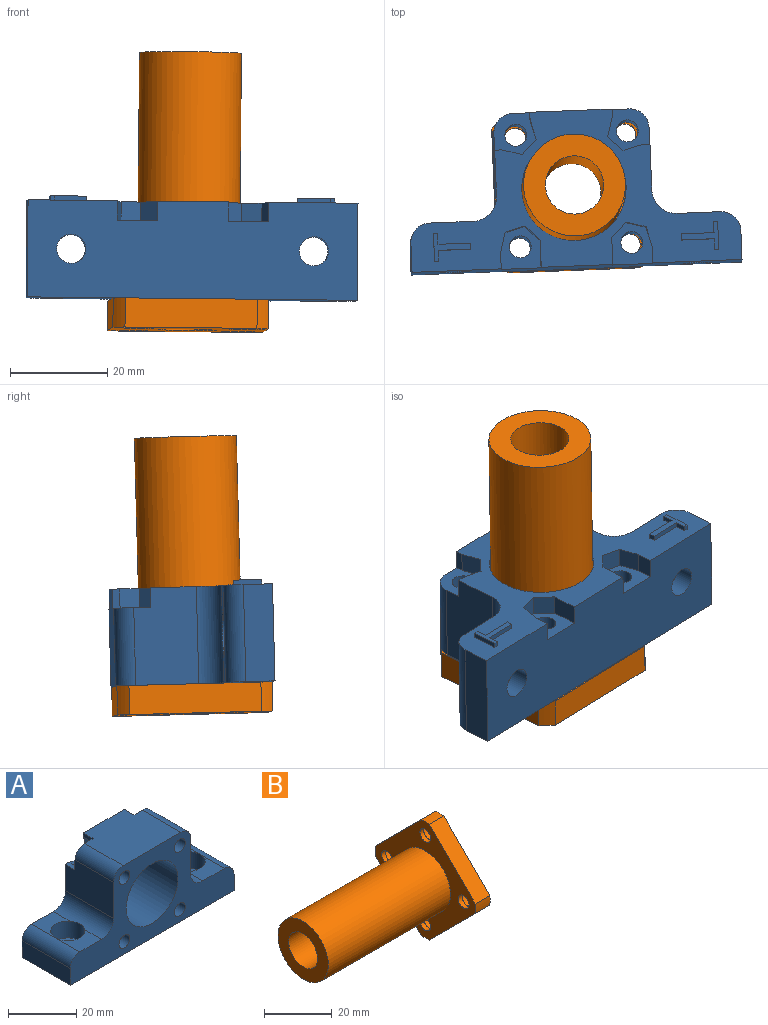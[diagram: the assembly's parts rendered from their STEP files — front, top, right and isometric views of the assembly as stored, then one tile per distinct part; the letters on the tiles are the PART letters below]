
ASSEMBLY  parts=2 mates=1
PART A: 70 faces, bbox 68x21x32 mm
  f0: cylinder r=4mm len=20mm, axis (0,-1,0), area 125.7mm2, adj f1,f2,f45,f51
  f1: plane 20x6mm, normal (1,0,0), area 120mm2, adj f0,f2,f37,f51
  f2: plane 68x32mm, normal (0,-1,0), area 954.3mm2, adj f0,f1,f3,f4,f5,f6,f7,f9
  f3: cylinder r=4mm len=20mm, axis (0,1,0), area 125.7mm2, adj f2,f4,f5,f14,f51
  f4: plane 10x9mm, normal (0,0,1), area 52.8mm2, adj f2,f3,f13,f41
  f5: plane 20x6mm, normal (-1,0,0), area 120mm2, adj f2,f3,f37,f51
  f6: cylinder r=4mm len=16mm, axis (0,1,0), area 100.5mm2, adj f2,f7,f8,f38
  f7: plane 24x20mm, normal (0,0,1), area 451.8mm2, adj f2,f6,f8,f9,f11,f29,f33,f51
  f8: plane 8.63x8.63mm, normal (0,1,0), area 42.7mm2, adj f6,f7,f32,f33,f34,f35,f36,f38
  f9: cylinder r=4mm len=16mm, axis (0,1,0), area 100.5mm2, adj f2,f7,f10,f11
  f10: plane 20x13mm, normal (-1,0,0), area 245.9mm2, adj f2,f9,f11,f13,f28,f51
  f11: plane 8.63x8.63mm, normal (0,1,0), area 42.7mm2, adj f7,f9,f10,f27,f28,f29,f30,f31
  f12: cylinder r=5mm len=20mm, axis (0,1,0), area 153mm2, adj f2,f38,f43,f45,f51
  f13: cylinder r=5mm len=20mm, axis (0,-1,0), area 154.1mm2, adj f2,f4,f10,f14,f41,f51
  f14: plane 10x9mm, normal (0,0,1), area 52.8mm2, adj f3,f13,f41,f51
  f15: plane 4.13x4mm, normal (0.26,0,-0.97), area 17.1mm2, adj f16,f19,f20,f51
  f16: plane 4x3.02mm, normal (-0.71,0,-0.71), area 17.1mm2, adj f15,f17,f20,f51
  f17: plane 5.61x4mm, normal (-1,0,0), area 22.4mm2, adj f16,f20,f37,f51
  f18: plane 4x3.39mm, normal (1,0,0), area 13.6mm2, adj f19,f20,f37,f51
  f19: plane 4.13x4mm, normal (0.97,0,-0.26), area 17.1mm2, adj f15,f18,f20,f51
  f20: plane 8.63x8.25mm, normal (0,1,0), area 44.9mm2, adj f15,f16,f17,f18,f19,f37,f46
  f21: plane 4.13x4mm, normal (-0.97,0,-0.26), area 17.1mm2, adj f22,f25,f26,f51
  f22: plane 4x3.39mm, normal (-1,0,0), area 13.6mm2, adj f21,f26,f37,f51
  f23: plane 5.61x4mm, normal (1,0,0), area 22.4mm2, adj f24,f26,f37,f51
  f24: plane 4x3.02mm, normal (0.71,0,-0.71), area 17.1mm2, adj f23,f25,f26,f51
  f25: plane 4.13x4mm, normal (-0.26,0,-0.97), area 17.1mm2, adj f21,f24,f26,f51
  f26: plane 8.63x8.25mm, normal (0,1,0), area 44.9mm2, adj f21,f22,f23,f24,f25,f37,f47
  f27: plane 4.13x4mm, normal (0.26,0,0.97), area 17.1mm2, adj f11,f28,f31,f51
  f28: plane 4x1.48mm, normal (0,0,1), area 5.9mm2, adj f10,f11,f27,f51
  f29: plane 4x1.48mm, normal (-1,0,0), area 5.9mm2, adj f7,f11,f30,f51
  f30: plane 4.13x4mm, normal (-0.97,0,-0.26), area 17.1mm2, adj f11,f29,f31,f51
  f31: plane 4x3.02mm, normal (-0.71,0,0.71), area 17.1mm2, adj f11,f27,f30,f51
  f32: plane 4.13x4mm, normal (0.97,0,-0.26), area 17.1mm2, adj f8,f33,f36,f51
  f33: plane 4x1.48mm, normal (1,0,0), area 5.9mm2, adj f7,f8,f32,f51
  f34: plane 4x1.48mm, normal (0,0,1), area 5.9mm2, adj f8,f35,f38,f51
  f35: plane 4.13x4mm, normal (-0.26,0,0.97), area 17.1mm2, adj f8,f34,f36,f51
  f36: plane 4x3.02mm, normal (0.71,0,0.71), area 17.1mm2, adj f8,f32,f35,f51
  f37: plane 68x20mm, normal (0,0,-1), area 1237.4mm2, adj f1,f2,f5,f17,f18,f20,f22,f23
  f38: plane 20x13mm, normal (1,0,0), area 245.9mm2, adj f2,f6,f8,f12,f34,f51
  f39: cylinder r=3mm len=6mm, axis (0,0,-1), area 75.4mm2, adj f37,f44
  f40: cylinder r=3mm len=6mm, axis (0,0,-1), area 75.4mm2, adj f37,f42
  f41: cylinder r=5mm len=10mm, axis (0,0,-1), area 188.8mm2, adj f4,f13,f14,f42
  f42: plane 10x10mm, normal (0,0,1), area 50.3mm2, adj f40,f41
  f43: cylinder r=5mm len=10mm, axis (0,0,-1), area 188.5mm2, adj f12,f44,f45
  f44: plane 10x10mm, normal (0,0,1), area 50.3mm2, adj f39,f43
  f45: plane 20x9mm, normal (0,0,1), area 105.5mm2, adj f0,f2,f12,f43,f51
  f46: cylinder r=2.25mm len=16mm, axis (0,1,0), area 226.2mm2, adj f2,f20
  f47: cylinder r=2.25mm len=16mm, axis (0,1,0), area 226.2mm2, adj f2,f26
  f48: cylinder r=10.75mm len=21.5mm, axis (0,1,0), area 1350.9mm2, adj f2,f51
  f49: cylinder r=2.25mm len=16mm, axis (0,1,0), area 226.2mm2, adj f2,f11
  f50: cylinder r=2.25mm len=16mm, axis (0,1,0), area 226.2mm2, adj f2,f8
  f51: plane 68x32mm, normal (0,1,0), area 752.6mm2, adj f0,f1,f3,f5,f7,f10,f12,f13
  f52: plane 1x0.84mm, normal (0,0,1), area 0.8mm2, adj f51,f53,f59,f60
  f53: plane 5.77x1mm, normal (1,0,0), area 5.8mm2, adj f51,f52,f54,f60
  f54: plane 1x0.84mm, normal (0,0,-1), area 0.8mm2, adj f51,f53,f55,f60
  f55: plane 2.26x1mm, normal (-1,0,0), area 2.3mm2, adj f51,f54,f56,f60
  f56: plane 6.74x1mm, normal (0,0,-1), area 6.7mm2, adj f51,f55,f57,f60
  f57: plane 1.24x1mm, normal (-1,0,0), area 1.2mm2, adj f51,f56,f58,f60
  f58: plane 6.74x1mm, normal (0,0,1), area 6.7mm2, adj f51,f57,f59,f60
  f59: plane 2.26x1mm, normal (-1,0,0), area 2.3mm2, adj f51,f52,f58,f60
  f60: plane 7.58x5.77mm, normal (0,1,0), area 13.2mm2, adj f52,f53,f54,f55,f56,f57,f58,f59
  f61: plane 1x0.84mm, normal (0,0,-1), area 0.8mm2, adj f51,f62,f68,f69
  f62: plane 5.77x1mm, normal (-1,0,0), area 5.8mm2, adj f51,f61,f63,f69
  f63: plane 1x0.84mm, normal (0,0,1), area 0.8mm2, adj f51,f62,f64,f69
  f64: plane 2.26x1mm, normal (1,0,0), area 2.3mm2, adj f51,f63,f65,f69
  f65: plane 6.74x1mm, normal (0,0,1), area 6.7mm2, adj f51,f64,f66,f69
  f66: plane 1.24x1mm, normal (1,0,0), area 1.2mm2, adj f51,f65,f67,f69
  f67: plane 6.74x1mm, normal (0,0,-1), area 6.7mm2, adj f51,f66,f68,f69
  f68: plane 2.26x1mm, normal (1,0,0), area 2.3mm2, adj f51,f61,f67,f69
  f69: plane 7.58x5.77mm, normal (0,1,0), area 13.2mm2, adj f61,f62,f63,f64,f65,f66,f67,f68
PART B: 25 faces, bbox 57x42x42 mm
  f0: plane 42x42mm, normal (1,0,0), area 699mm2, adj f1,f2,f3,f4,f7,f9,f12,f15
  f1: cylinder r=21mm len=6mm, axis (1,0,0), area 20.4mm2, adj f0,f5,f21,f24
  f2: cylinder r=21mm len=6mm, axis (1,0,0), area 20.4mm2, adj f0,f5,f23,f24
  f3: cylinder r=21mm len=6mm, axis (1,0,0), area 20.4mm2, adj f0,f5,f22,f23
  f4: cylinder r=21mm len=6mm, axis (1,0,0), area 20.4mm2, adj f0,f5,f21,f22
  f5: plane 42x42mm, normal (-1,0,0), area 603.1mm2, adj f1,f2,f3,f4,f8,f11,f14,f17
  f6: plane 21x21mm, normal (-1,0,0), area 233.3mm2, adj f7,f8
  f7: cylinder r=6mm len=57mm, axis (1,0,0), area 2148.8mm2, adj f0,f6
  f8: cylinder r=10.5mm len=51mm, axis (1,0,0), area 3364.6mm2, adj f5,f6
  f9: cylinder r=4mm len=8mm, axis (-1,0,0), area 110.6mm2, adj f0,f10
  f10: plane 8x8mm, normal (1,0,0), area 34.4mm2, adj f9,f11
  f11: cylinder r=2.25mm len=4.5mm, axis (-1,0,0), area 22.6mm2, adj f5,f10
  f12: cylinder r=4mm len=8mm, axis (-1,0,0), area 110.6mm2, adj f0,f13
  f13: plane 8x8mm, normal (1,0,0), area 34.4mm2, adj f12,f14
  f14: cylinder r=2.25mm len=4.5mm, axis (-1,0,0), area 22.6mm2, adj f5,f13
  f15: cylinder r=4mm len=8mm, axis (-1,0,0), area 110.6mm2, adj f0,f16
  f16: plane 8x8mm, normal (1,0,0), area 34.4mm2, adj f15,f17
  f17: cylinder r=2.25mm len=4.5mm, axis (-1,0,0), area 22.6mm2, adj f5,f16
  f18: cylinder r=4mm len=8mm, axis (-1,0,0), area 110.6mm2, adj f0,f19
  f19: plane 8x8mm, normal (1,0,0), area 34.4mm2, adj f18,f20
  f20: cylinder r=2.25mm len=4.5mm, axis (-1,0,0), area 22.6mm2, adj f5,f19
  f21: plane 19.24x19.24mm, normal (0,-0.71,0.71), area 163.2mm2, adj f0,f1,f4,f5
  f22: plane 19.24x19.24mm, normal (0,-0.71,-0.71), area 163.2mm2, adj f0,f3,f4,f5
  f23: plane 19.24x19.24mm, normal (0,0.71,-0.71), area 163.2mm2, adj f0,f2,f3,f5
  f24: plane 19.24x19.24mm, normal (0,0.71,0.71), area 163.2mm2, adj f0,f1,f2,f5
PLACE A rot(axis=(0.01,-0.72,-0.7),178deg) t=(202,-1056.57,34.26)mm
PLACE B rot(axis=(0.33,0.87,-0.36),97.6deg) t=(204.67,-304.99,65.37)mm
MATE fastened B.f12 <-> A.f47  axis (0.01,0.03,1) through (193.33,-318.09,14.81)mm
